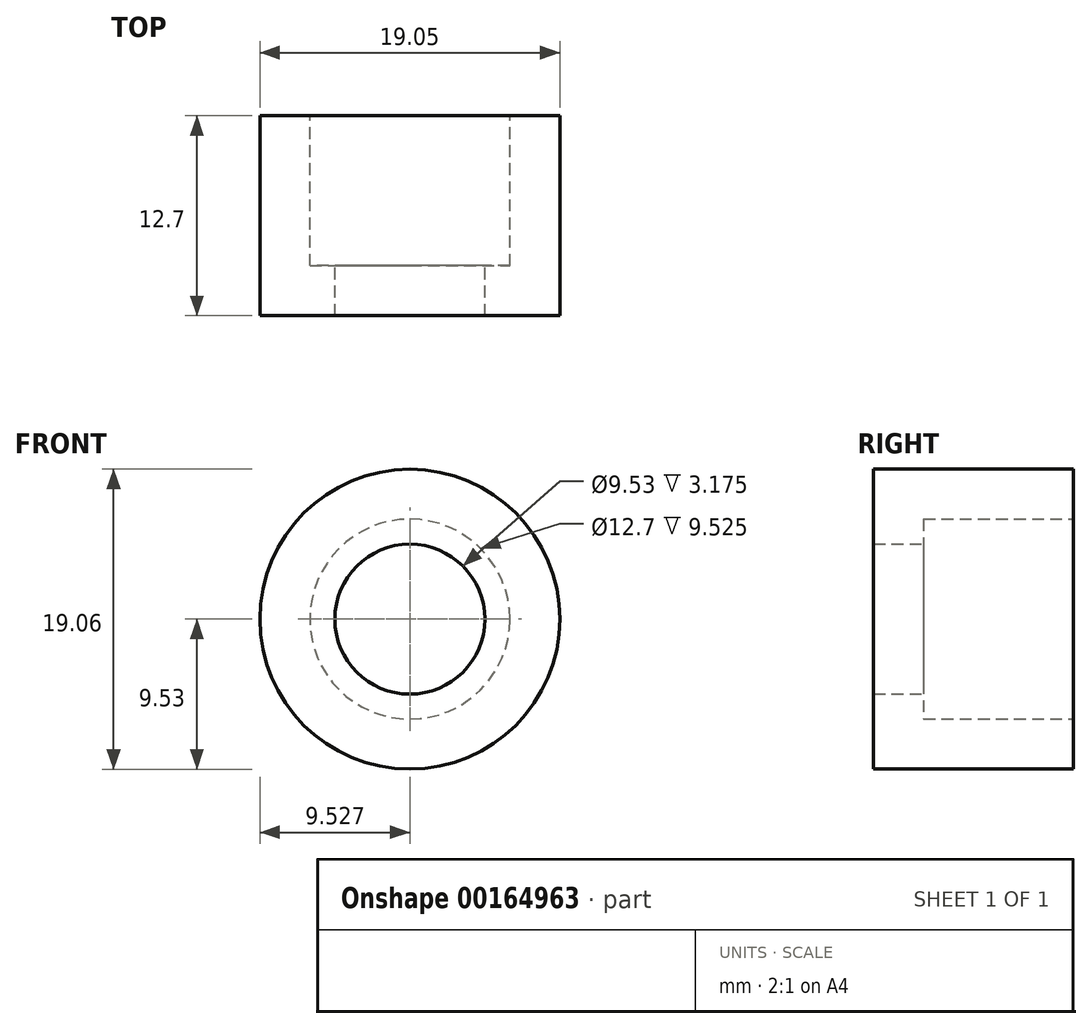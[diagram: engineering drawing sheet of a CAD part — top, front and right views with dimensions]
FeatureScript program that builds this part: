
annotation { "Feature Type Name" : "Feature", "Feature Type Description" : "" }
export const myFeature = defineFeature(function(context is Context, id is Id, definition is map)
    precondition{}
    {
        {
            var Q0;
            Q0=qCreatedBy(makeId("Top.planeOp"),FACE);
            var sketch = newSketch(context, id + "F0", { "sketchPlane" : qUnion([Q0])});
            skLineSegment(sketch, "E0.top", {"start": v(1.59, 3.18) * mm, "end": v(0, 3.18) * mm});
            skLineSegment(sketch, "E0.right", {"start": v(0, 0) * mm, "end": v(0, 3.18) * mm});
            skLineSegment(sketch, "E1.bottom", {"start": v(1.59, 12.7) * mm, "end": v(4.76, 12.7) * mm});
            skLineSegment(sketch, "E1.top", {"start": v(0, 0) * mm, "end": v(4.76, 0) * mm});
            skLineSegment(sketch, "E1.right", {"start": v(4.76, 12.7) * mm, "end": v(4.76, 0) * mm});
            skLineSegment(sketch, "E2", {"start": v(1.59, 3.18) * mm, "end": v(1.59, 12.7) * mm});
            skLineSegment(sketch, "E3", {"start": v(0, 1.59) * mm, "end": v(-4.76, 1.59) * mm, "construction": true});
            skLineSegment(sketch, "E4", {"start": v(-4.76, 1.59) * mm, "end": v(-4.76, 0) * mm, "construction": true});
            skLineSegment(sketch, "E5", {"start": v(-4.76, 0) * mm, "end": v(0, 0) * mm, "construction": true});
            skSolve(sketch);
        }
        {
            var Q0;
            Q0 = qSketchRegion(id + "F0", true);
            var Q1;
            Q1=sQuery(id+"F0.wireOp",EDGE,"E4");
            revolve(context, id + "F1", {"entities" : qUnion([Q0]), "axis" : qUnion([Q1]), "revolveType" : RevolveType.FULL});
        }
    });
